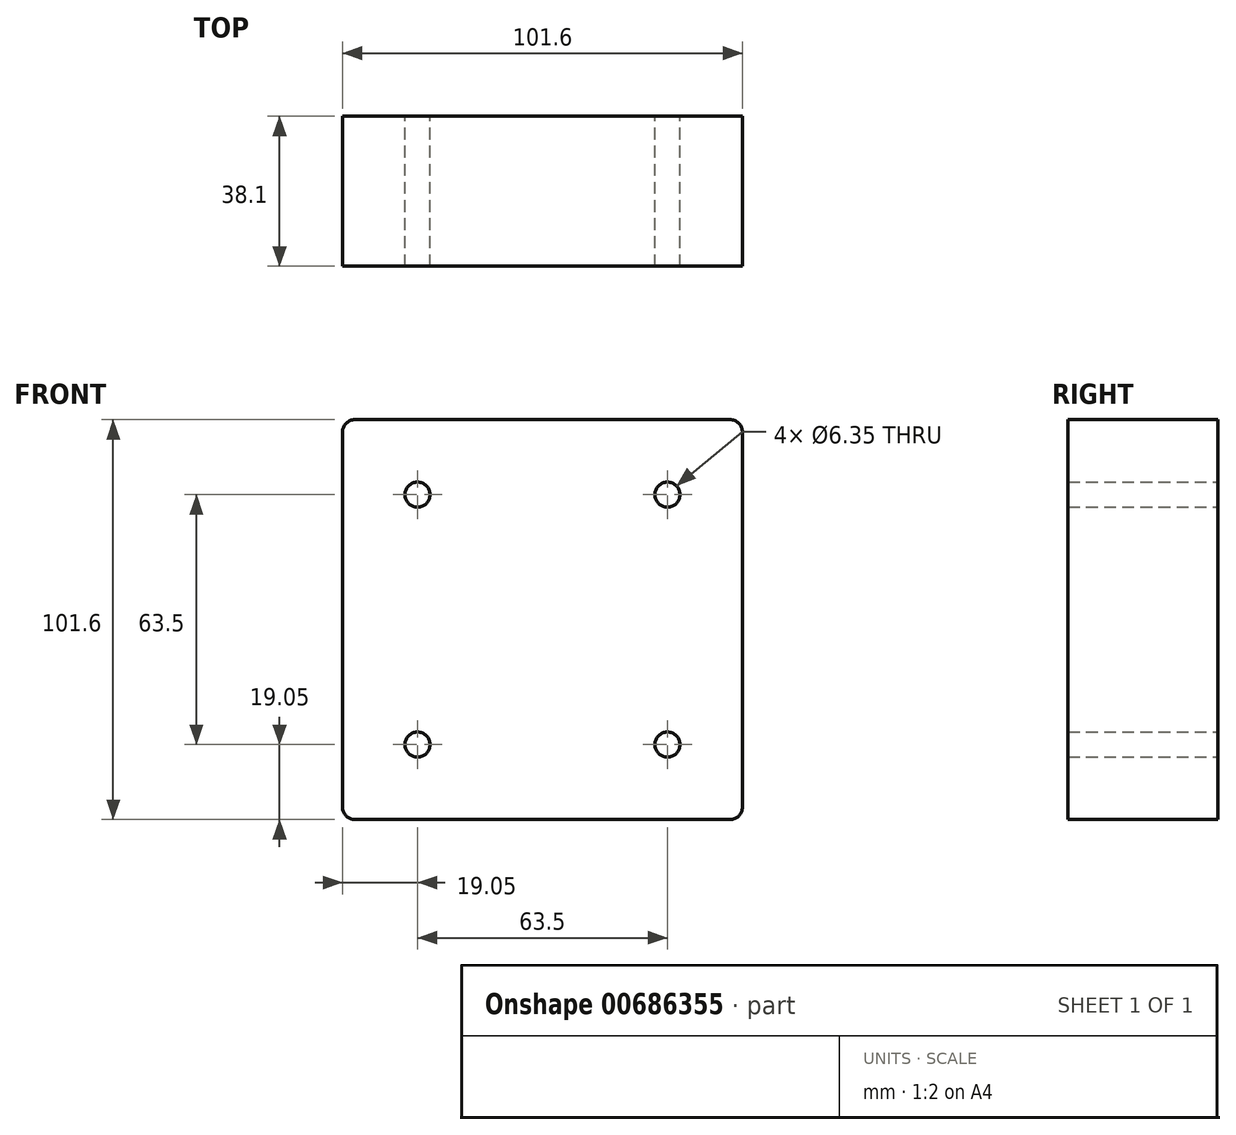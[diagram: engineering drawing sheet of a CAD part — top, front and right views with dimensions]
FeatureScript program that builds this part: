
annotation { "Feature Type Name" : "Feature", "Feature Type Description" : "" }
export const myFeature = defineFeature(function(context is Context, id is Id, definition is map)
    precondition{}
    {
        {
            var Q0;
            Q0=qCreatedBy(makeId("Front.planeOp"),FACE);
            var sketch = newSketch(context, id + "F0", { "sketchPlane" : qUnion([Q0])});
            skLineSegment(sketch, "E0.bottom", {"start": v(3.17, 101.6) * mm, "end": v(98.42, 101.6) * mm});
            skLineSegment(sketch, "E0.top", {"start": v(3.17, 0) * mm, "end": v(98.43, 0) * mm});
            skLineSegment(sketch, "E0.left", {"start": v(0, 98.42) * mm, "end": v(0, 3.18) * mm});
            skLineSegment(sketch, "E0.right", {"start": v(101.6, 98.42) * mm, "end": v(101.6, 3.18) * mm});
            skCircle(sketch, "E1", {"center": v(19.05, 19.05) * mm, "radius": 3.18 * mm});
            skCircle(sketch, "E2", {"center": v(82.55, 19.05) * mm, "radius": 3.18 * mm});
            skCircle(sketch, "E3.MirrorC", {"center": v(82.55, 82.55) * mm, "radius": 3.18 * mm});
            skCircle(sketch, "E4.MirrorC", {"center": v(19.05, 82.55) * mm, "radius": 3.18 * mm});
            skPoint(sketch, "E5.visualSharp", {"position": v(0, 101.6) * mm});
            skArc(sketch, "E5.filletArc", {"start": v(3.17, 101.6) * mm, "mid": v(0.93, 100.67) * mm, "end": v(0, 98.42) * mm});
            skPoint(sketch, "E6.visualSharp", {"position": v(0, 0) * mm});
            skArc(sketch, "E6.filletArc", {"start": v(0, 3.18) * mm, "mid": v(0.93, 0.93) * mm, "end": v(3.17, 0) * mm});
            skPoint(sketch, "E7.visualSharp", {"position": v(101.6, 0) * mm});
            skArc(sketch, "E7.filletArc", {"start": v(98.43, 0) * mm, "mid": v(100.67, 0.93) * mm, "end": v(101.6, 3.18) * mm});
            skPoint(sketch, "E8.visualSharp", {"position": v(101.6, 101.6) * mm});
            skArc(sketch, "E8.filletArc", {"start": v(101.6, 98.42) * mm, "mid": v(100.67, 100.67) * mm, "end": v(98.42, 101.6) * mm});
            skSolve(sketch);
        }
        {
            var Q0;
            Q0=makeQuery(id+"F0.imprint","IMPRINT",FACE,{"disambiguationData":[TD([[makeQuery(id+"F0.imprint","IMPRINT",EDGE,{"derivedFrom":sQuery(id+"F0.wireOp",EDGE,"E0.bottom")}),-1.0]])]});
            extrude(context, id + "F1", {"entities" : qUnion([Q0]), "depth" : 38.1 * mm, "offsetDistance" : 25.4 * mm});
        }
    });
